# Revit family: LeL Reiko 4.0
name_source: partatom
category: Lighting Fixtures
units: mm (PartAtom-declared; Revit-internal decimal feet)

## family parameters
Always vertical = No
Cut with Voids When Loaded = No
Light Source = No
OmniClass Number = 23.80.70.00
OmniClass Title = Lighting
Part Type = Normal
Room Calculation Point = No
Round Connector Dimension = Use Diameter
Shared = No
Work Plane-Based = Yes

## types (7) — shared parameters
Apparent Load = 25 VA
CCT = 3000 K
CRI = CRI80
Default Elevation = 1219 mm
Description = Outdoor Projectors
IK = IK06
IP = IP66
Lamp = LED
Manufacturer = L&L Luce&Light srl
Model = RK40
Rated Power supply = 24 V
URL = https://www.lucelight.it
Wattage = 25 W
Weight = 2.25 kg

## per-type parameters (varying)
| type | Lumen Output | Photometry |
| K 55° 25W | 1838 lm | RK40 Light source : K 55° 25W |
| L 38° 25W | 2032 lm | RK40 Light source : L 38° 25W |
| M 27° 25W | 2051 lm | RK40 Light source : M 27° 25W |
| P (33°) 25W | 895 lm | RK40 Light source : P (33°) 25W |
| S 13° 25W | 2128 lm | RK40 Light source : S 13° 25W |
| W 13°x66° 25W | 1962 lm | RK40 Light source : W 13°x66° 25W |
| X 25°x68° 25W | 1962 lm | RK40 Light source : X 25°x68° 25W |

## geometry (parser evidence)
native form markers: Sweep x3
no freeform markers — native parametric forms only
